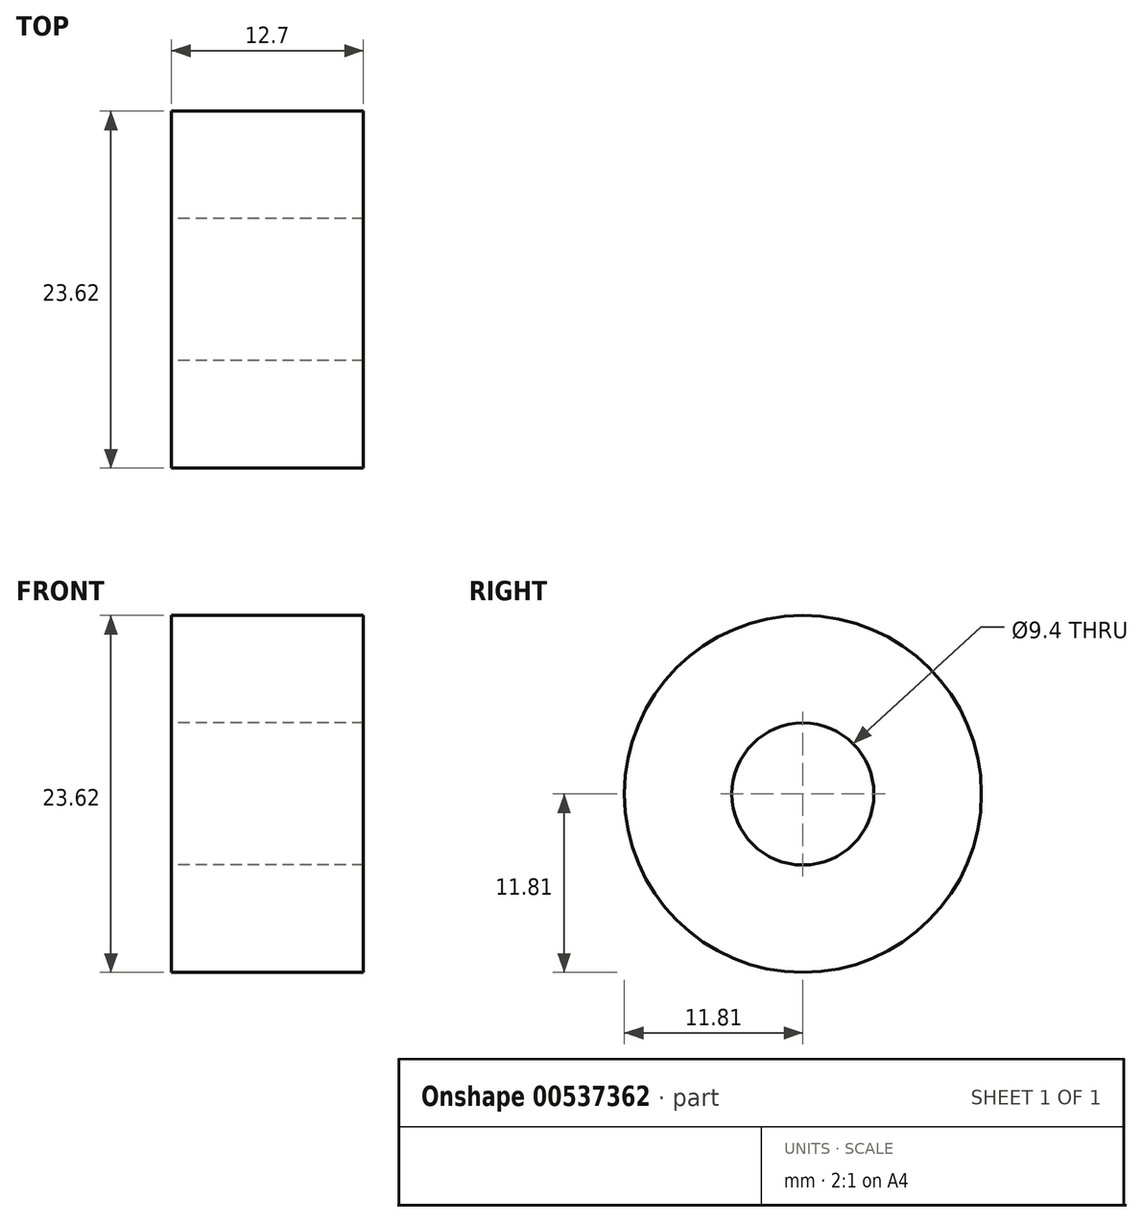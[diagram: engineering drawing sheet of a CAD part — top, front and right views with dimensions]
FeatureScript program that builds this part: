
annotation { "Feature Type Name" : "Feature", "Feature Type Description" : "" }
export const myFeature = defineFeature(function(context is Context, id is Id, definition is map)
    precondition{}
    {
        {
            var Q0;
            Q0=qCreatedBy(makeId("Right.planeOp"),FACE);
            var sketch = newSketch(context, id + "F0", { "sketchPlane" : qUnion([Q0])});
            skCircle(sketch, "E0", {"center": v(0, 0) * mm, "radius": 11.81 * mm});
            skCircle(sketch, "E1", {"center": v(0, 0) * mm, "radius": 4.7 * mm});
            skSolve(sketch);
        }
        {
            var Q0;
            Q0 = qSketchRegion(id + "F0", true);
            extrude(context, id + "F1", {"entities" : qUnion([Q0]), "depth" : 12.7 * mm, "offsetDistance" : 25.4 * mm});
        }
    });
